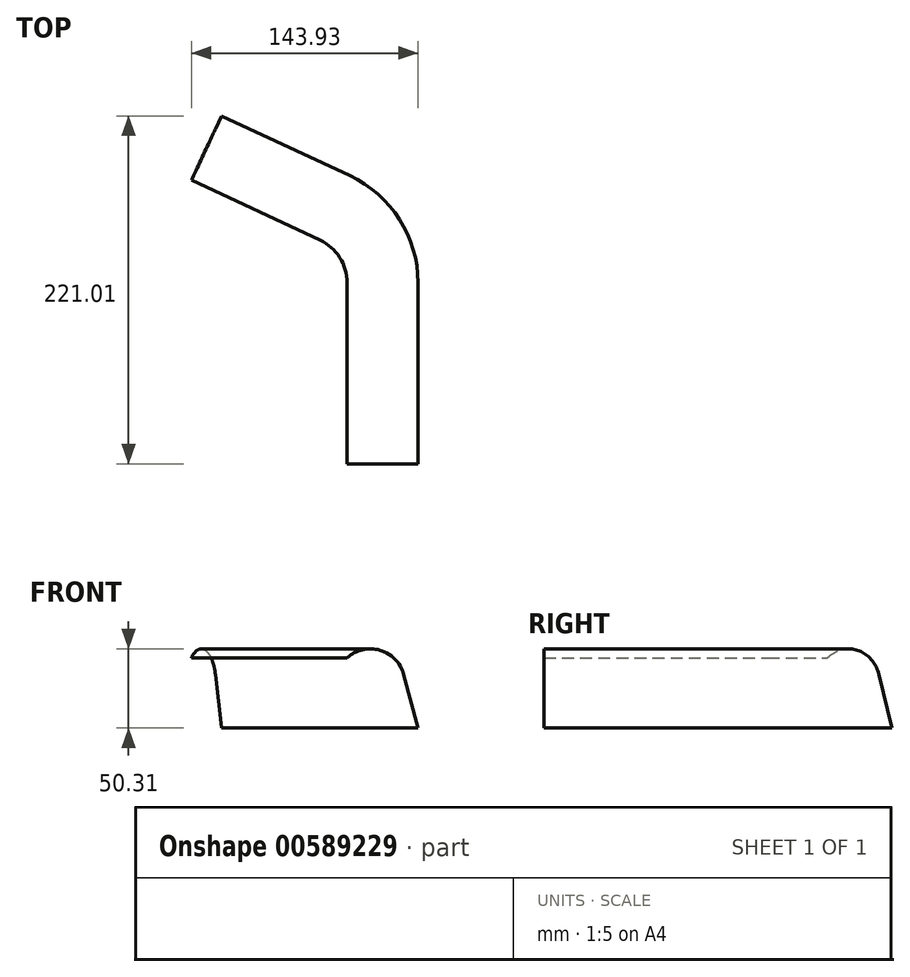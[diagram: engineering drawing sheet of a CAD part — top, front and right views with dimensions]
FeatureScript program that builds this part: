
annotation { "Feature Type Name" : "Feature", "Feature Type Description" : "" }
export const myFeature = defineFeature(function(context is Context, id is Id, definition is map)
    precondition{}
    {
        {
            var Q0;
            Q0=qCreatedBy(makeId("Top.planeOp"),FACE);
            var sketch = newSketch(context, id + "F0", { "sketchPlane" : qUnion([Q0])});
            skLineSegment(sketch, "E0", {"start": v(0, -115) * mm, "end": v(0, 0) * mm});
            skArc(sketch, "E1", {"start": v(0, 0) * mm, "mid": v(-11.75, 40.3) * mm, "end": v(-43.3, 67.97) * mm});
            skLineSegment(sketch, "E2", {"start": v(-43.3, 67.97) * mm, "end": v(-124.87, 106) * mm});
            skSolve(sketch);
        }
        {
            var Q0;
            Q0=sQuery(id+"F0.wireOp",VERTEX,"E0.start");
            var Q1;
            Q1=sQuery(id+"F0.wireOp",EDGE,"E0");
            cPlane(context, id + "F1", {"entities" : qUnion([Q0, Q1]), "cplaneType" : CPlaneType.CURVE_POINT, "offset" : 25 * mm, "width" : 150 * mm, "height" : 150 * mm});
        }
        {
            var Q0;
            Q0=qCreatedBy(id+"F1.planeOp",FACE);
            var sketch = newSketch(context, id + "F2", { "sketchPlane" : qUnion([Q0])});
            skLineSegment(sketch, "E3", {"start": v(0, 0) * mm, "end": v(9.11, 34) * mm});
            skArc(sketch, "E4", {"start": v(45.1, 44.65) * mm, "mid": v(24.12, 49.4) * mm, "end": v(9.11, 34) * mm});
            skSolve(sketch);
        }
        {
            var Q0;
            Q0 = qSketchRegion(id + "F2", true);
            var Q1;
            Q1 = qConstructionFilter(qBodyType(qCreatedBy(id + "F2" ,EDGE), BodyType.WIRE), ConstructionObject.NO);
            var Q2;
            Q2 = qConstructionFilter(qBodyType(qCreatedBy(id + "F0" ,EDGE), BodyType.WIRE), ConstructionObject.NO);
            sweep(context, id + "F3", {"bodyType" : ToolBodyType.SURFACE, "profiles" : qUnion([Q0]), "surfaceProfiles" : qUnion([Q1]), "path" : qUnion([Q2])});
        }
    });
